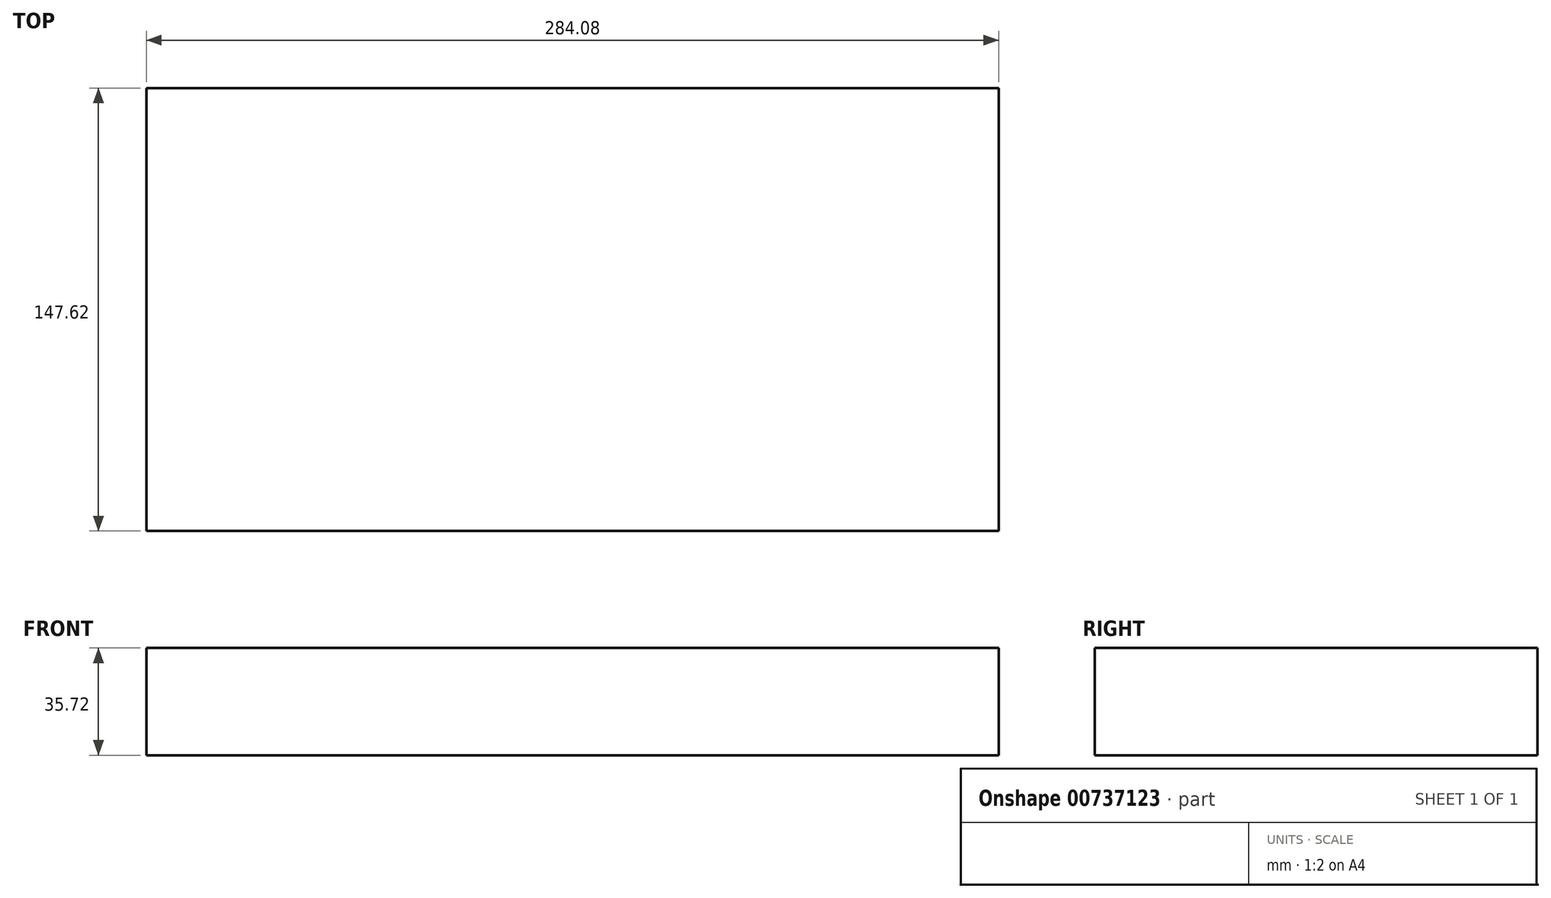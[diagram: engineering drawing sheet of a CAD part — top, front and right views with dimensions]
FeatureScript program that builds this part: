
annotation { "Feature Type Name" : "Feature", "Feature Type Description" : "" }
export const myFeature = defineFeature(function(context is Context, id is Id, definition is map)
    precondition{}
    {
        {
            var Q0;
            Q0=qCreatedBy(makeId("Top.planeOp"),FACE);
            var sketch = newSketch(context, id + "F0", { "sketchPlane" : qUnion([Q0])});
            skLineSegment(sketch, "E0.bottom", {"start": v(142.04, -73.81) * mm, "end": v(-142.04, -73.81) * mm});
            skLineSegment(sketch, "E0.top", {"start": v(142.04, 73.81) * mm, "end": v(-142.04, 73.81) * mm});
            skLineSegment(sketch, "E0.left", {"start": v(142.04, -73.81) * mm, "end": v(142.04, 73.81) * mm});
            skLineSegment(sketch, "E0.right", {"start": v(-142.04, -73.81) * mm, "end": v(-142.04, 73.81) * mm});
            skPoint(sketch, "E0.middle", {"position": v(0, 0) * mm});
            skSolve(sketch);
        }
        {
            var Q0;
            Q0=makeQuery(id+"F0.imprint","IMPRINT",FACE,{"disambiguationData":[TD([[makeQuery(id+"F0.imprint","IMPRINT",EDGE,{"derivedFrom":sQuery(id+"F0.wireOp",EDGE,"E0.bottom")}),-1.0]])]});
            extrude(context, id + "F1", {"entities" : qUnion([Q0]), "depth" : 35.72 * mm, "offsetDistance" : 25.4 * mm});
        }
    });
